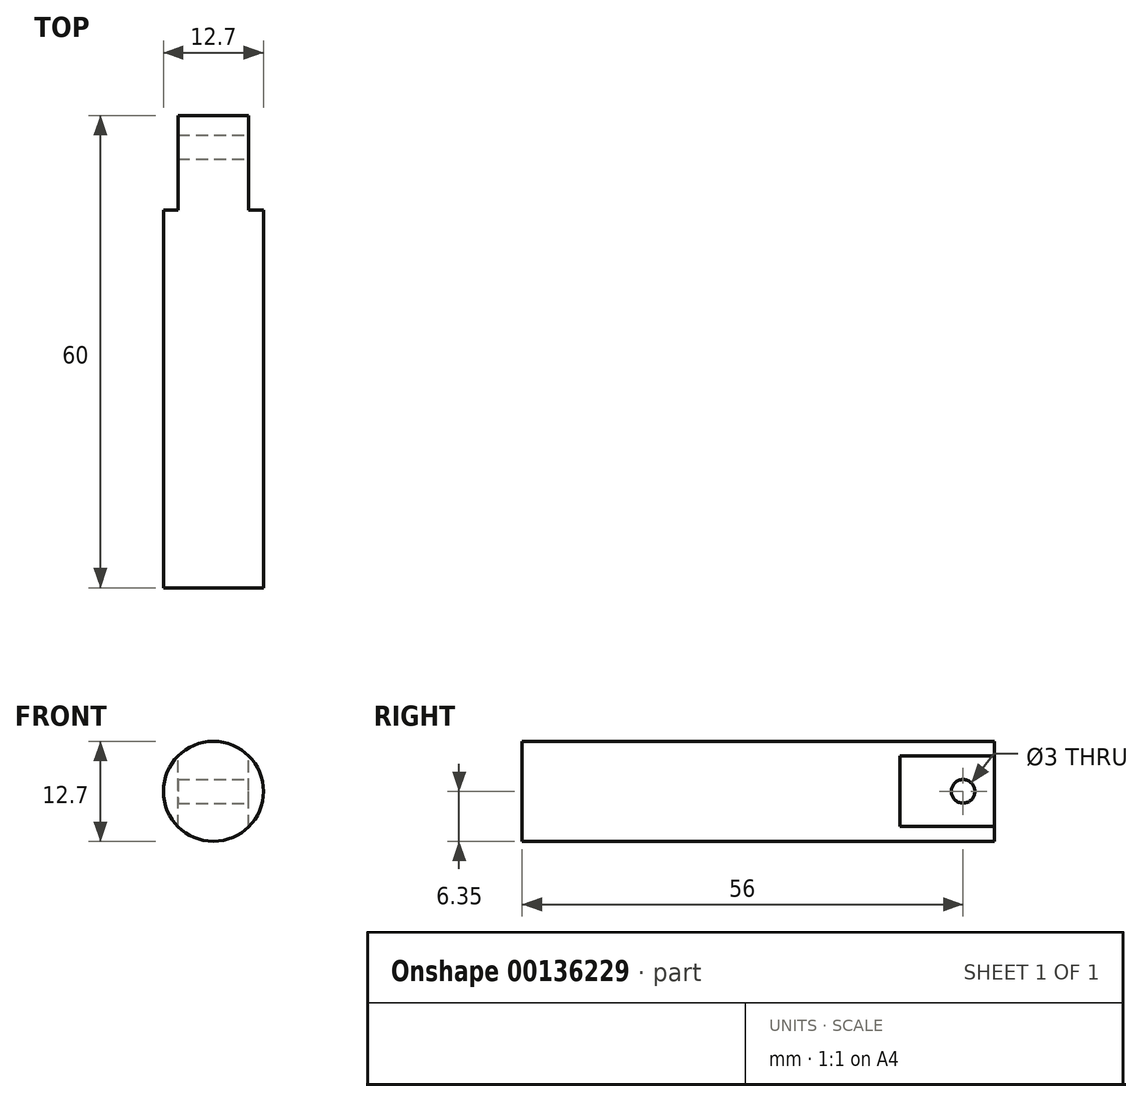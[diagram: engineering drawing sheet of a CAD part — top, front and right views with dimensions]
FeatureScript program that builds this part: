
annotation { "Feature Type Name" : "Feature", "Feature Type Description" : "" }
export const myFeature = defineFeature(function(context is Context, id is Id, definition is map)
    precondition{}
    {
        {
            var Q0;
            Q0=qCreatedBy(makeId("Front.planeOp"),FACE);
            var sketch = newSketch(context, id + "F0", { "sketchPlane" : qUnion([Q0])});
            skCircle(sketch, "E0", {"center": v(0, 0) * mm, "radius": 6.35 * mm});
            skSolve(sketch);
        }
        {
            var Q0;
            Q0 = qSketchRegion(id + "F0", true);
            extrude(context, id + "F1", {"entities" : qUnion([Q0]), "oppositeDirection" : true, "depth" : 60 * mm});
        }
        {
            var Q0;
            Q0=makeQuery(id+"F1.opExtrude","CAP_FACE",FACE,{"disambiguationData":[OSD([sQuery(id+"F0.wireOp",EDGE,"E0")])],"isStart":false});
            var sketch = newSketch(context, id + "F2", { "sketchPlane" : qUnion([Q0])});
            skLineSegment(sketch, "E1", {"start": v(0, 9.74) * mm, "end": v(0, -9.56) * mm, "construction": true});
            skLineSegment(sketch, "E2", {"start": v(-4.5, -7.19) * mm, "end": v(-4.5, 7.37) * mm});
            skLineSegment(sketch, "E3.MirrorCS", {"start": v(4.5, -7.19) * mm, "end": v(4.5, 7.37) * mm});
            skLineSegment(sketch, "E4", {"start": v(-4.5, -7.19) * mm, "end": v(-6.96, 0) * mm});
            skLineSegment(sketch, "E5", {"start": v(-6.96, 0) * mm, "end": v(-4.5, 7.37) * mm});
            skLineSegment(sketch, "E6.MirrorCS", {"start": v(4.5, -7.19) * mm, "end": v(6.96, 0) * mm});
            skLineSegment(sketch, "E7.MirrorCS", {"start": v(6.96, 0) * mm, "end": v(4.5, 7.37) * mm});
            skSolve(sketch);
        }
        {
            var Q0;
            Q0 = qSketchRegion(id + "F2", true);
            extrude(context, id + "F3", {"entities" : qUnion([Q0]), "operationType" : NewBodyOperationType.REMOVE, "oppositeDirection" : true, "depth" : 12 * mm});
        }
        {
            var Q0;
            Q0=makeQuery(id+"F3.boolean.opBoolean","COPY",FACE,{"derivedFrom":makeQuery(id+"F3.opExtrude","SWEPT_FACE",FACE,{"disambiguationData":[OSD([sQuery(id+"F2.wireOp",EDGE,"E2")])]})});
            var sketch = newSketch(context, id + "F4", { "sketchPlane" : qUnion([Q0])});
            skCircle(sketch, "E8", {"center": v(56, 0) * mm, "radius": 1.5 * mm});
            skPoint(sketch, "E8.centerSnap0", {"position": v(60, 0) * mm});
            skSolve(sketch);
        }
        {
            var Q0;
            Q0 = qSketchRegion(id + "F4", true);
            extrude(context, id + "F5", {"entities" : qUnion([Q0]), "operationType" : NewBodyOperationType.REMOVE, "oppositeDirection" : true, "depth" : 25 * mm});
        }
    });
